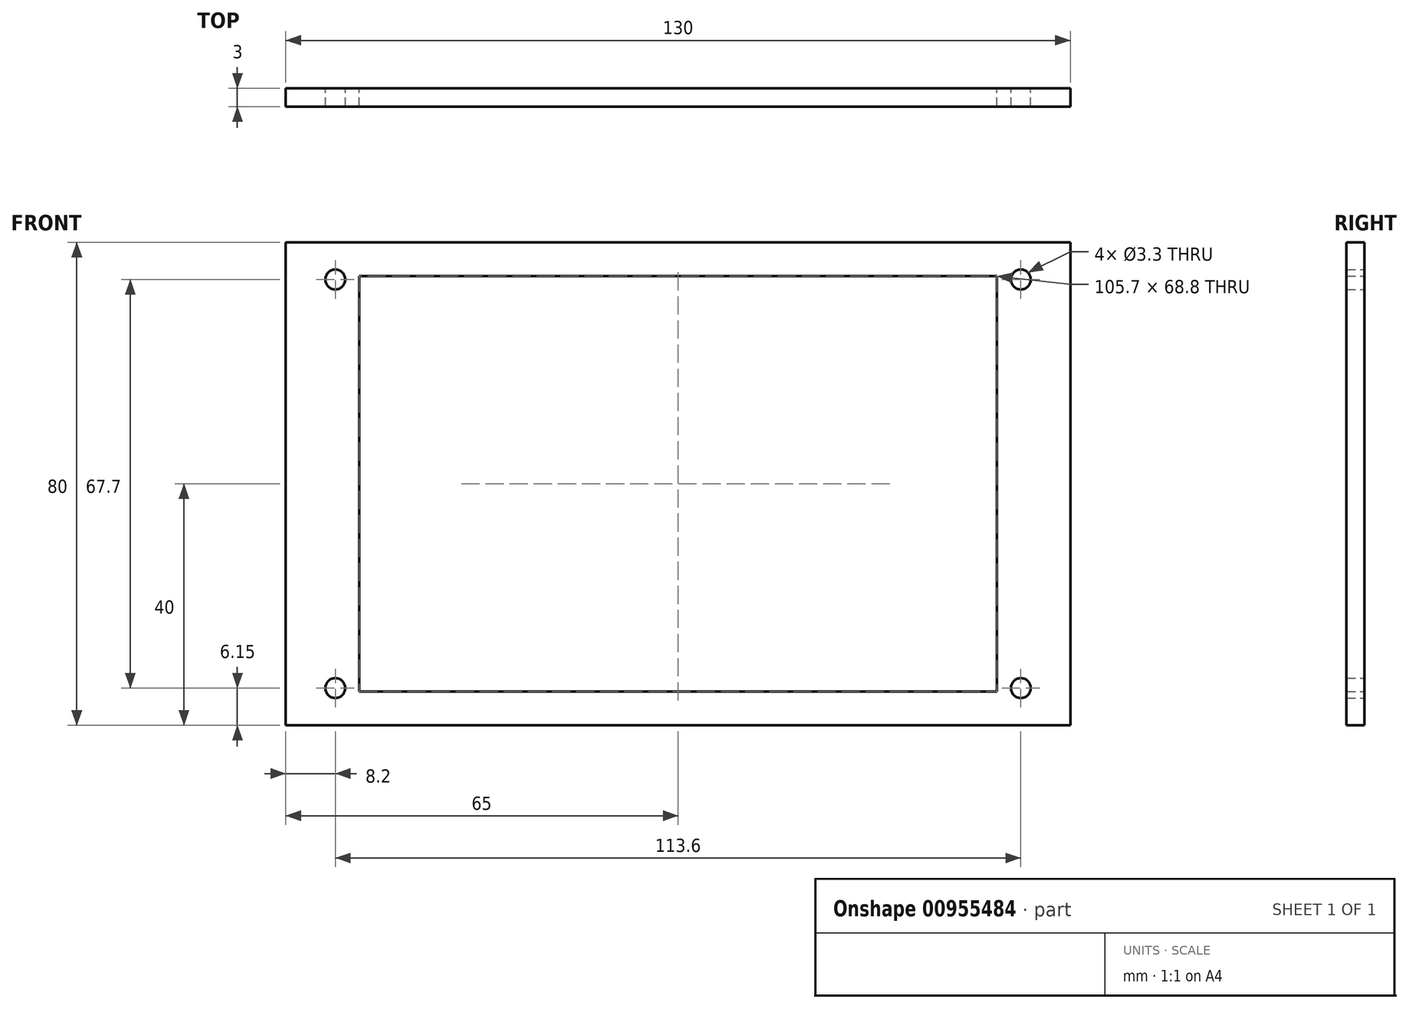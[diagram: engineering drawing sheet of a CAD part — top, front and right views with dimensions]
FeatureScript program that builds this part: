
annotation { "Feature Type Name" : "Feature", "Feature Type Description" : "" }
export const myFeature = defineFeature(function(context is Context, id is Id, definition is map)
    precondition{}
    {
        {
            var Q0;
            Q0=qCreatedBy(makeId("Front.planeOp"),FACE);
            var sketch = newSketch(context, id + "F0", { "sketchPlane" : qUnion([Q0])});
            skLineSegment(sketch, "E0.bottom", {"start": v(52.85, -34.4) * mm, "end": v(-52.85, -34.4) * mm});
            skLineSegment(sketch, "E0.top", {"start": v(52.85, 34.4) * mm, "end": v(-52.85, 34.4) * mm});
            skLineSegment(sketch, "E0.left", {"start": v(52.85, -34.4) * mm, "end": v(52.85, 34.4) * mm});
            skLineSegment(sketch, "E0.right", {"start": v(-52.85, -34.4) * mm, "end": v(-52.85, 34.4) * mm});
            skPoint(sketch, "E0.middle", {"position": v(0, 0) * mm});
            skLineSegment(sketch, "E1.bottom", {"start": v(65, -40) * mm, "end": v(-65, -40) * mm});
            skLineSegment(sketch, "E1.top", {"start": v(65, 40) * mm, "end": v(-65, 40) * mm});
            skLineSegment(sketch, "E1.left", {"start": v(65, -40) * mm, "end": v(65, 40) * mm});
            skLineSegment(sketch, "E1.right", {"start": v(-65, -40) * mm, "end": v(-65, 40) * mm});
            skLineSegment(sketch, "E2.bottom", {"start": v(56.8, 33.85) * mm, "end": v(-56.8, 33.85) * mm, "construction": true});
            skLineSegment(sketch, "E2.top", {"start": v(56.8, -33.85) * mm, "end": v(-56.8, -33.85) * mm, "construction": true});
            skLineSegment(sketch, "E2.left", {"start": v(56.8, 33.85) * mm, "end": v(56.8, -33.85) * mm, "construction": true});
            skLineSegment(sketch, "E2.right", {"start": v(-56.8, 33.85) * mm, "end": v(-56.8, -33.85) * mm, "construction": true});
            skCircle(sketch, "E3", {"center": v(-56.8, 33.85) * mm, "radius": 1.65 * mm});
            skCircle(sketch, "E4", {"center": v(-56.8, -33.85) * mm, "radius": 1.65 * mm});
            skCircle(sketch, "E5", {"center": v(56.8, -33.85) * mm, "radius": 1.65 * mm});
            skCircle(sketch, "E6", {"center": v(56.8, 33.85) * mm, "radius": 1.65 * mm});
            skSolve(sketch);
        }
        {
            var Q0;
            Q0 = qSketchRegion(id + "F0", true);
            extrude(context, id + "F1", {"entities" : qUnion([Q0]), "depth" : 3 * mm, "offsetDistance" : 25 * mm});
        }
    });
